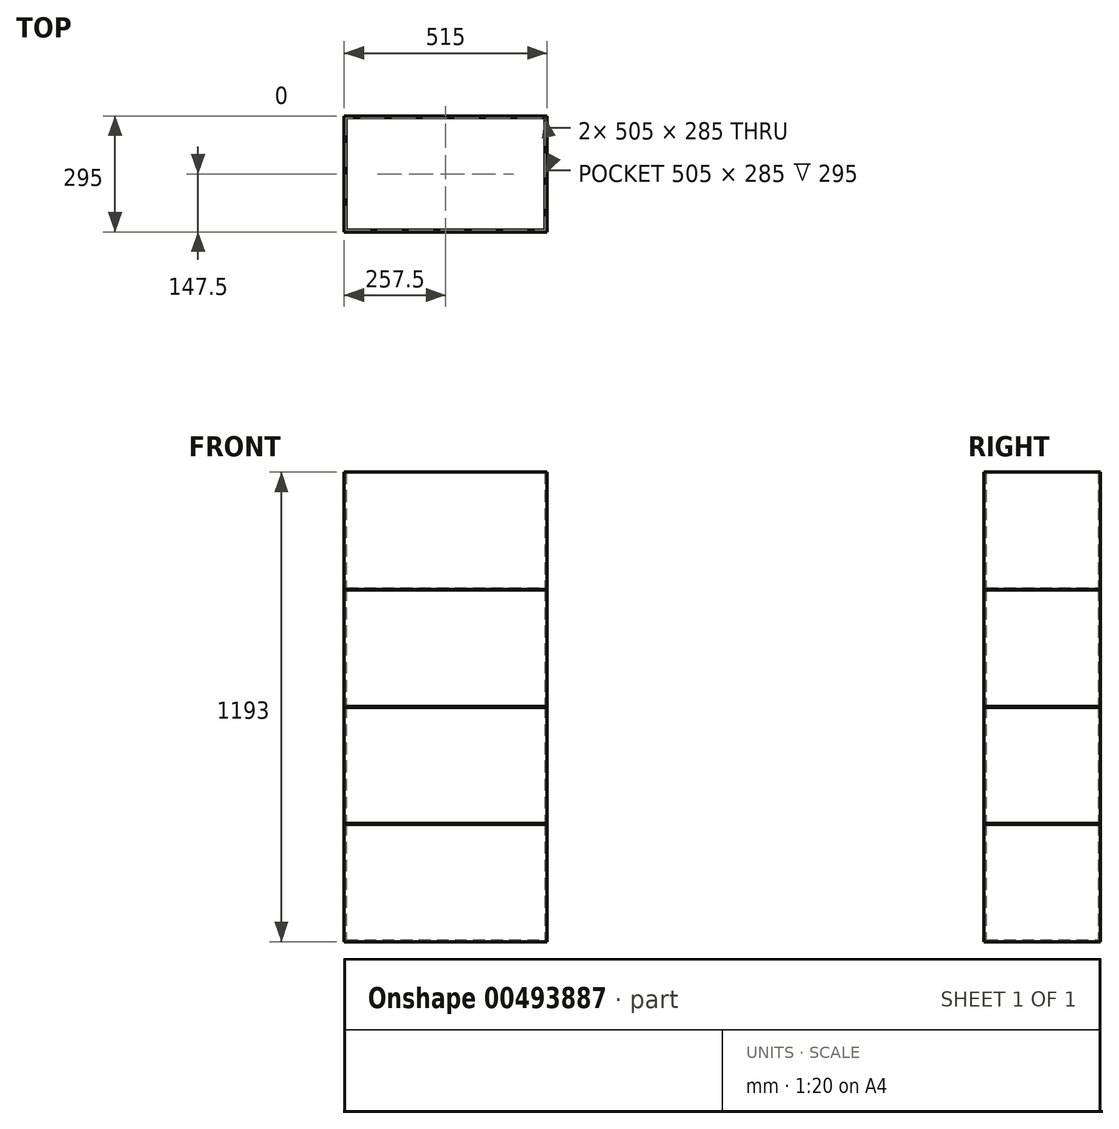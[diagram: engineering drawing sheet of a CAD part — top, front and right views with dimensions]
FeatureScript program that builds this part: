
annotation { "Feature Type Name" : "Feature", "Feature Type Description" : "" }
export const myFeature = defineFeature(function(context is Context, id is Id, definition is map)
    precondition{}
    {
        {
            var Q0;
            Q0=qCreatedBy(makeId("Top.planeOp"),FACE);
            var sketch = newSketch(context, id + "F0", { "sketchPlane" : qUnion([Q0])});
            skLineSegment(sketch, "E0.bottom", {"start": v(-257.5, -147.5) * mm, "end": v(257.5, -147.5) * mm});
            skLineSegment(sketch, "E0.top", {"start": v(-257.5, 147.5) * mm, "end": v(257.5, 147.5) * mm});
            skLineSegment(sketch, "E0.left", {"start": v(-257.5, -147.5) * mm, "end": v(-257.5, 147.5) * mm});
            skLineSegment(sketch, "E0.right", {"start": v(257.5, -147.5) * mm, "end": v(257.5, 147.5) * mm});
            skPoint(sketch, "E0.middle", {"position": v(0, 0) * mm});
            skSolve(sketch);
        }
        {
            var Q0;
            Q0=makeQuery(id+"F0.imprint","IMPRINT",FACE,{"disambiguationData":[TD([[makeQuery(id+"F0.imprint","IMPRINT",EDGE,{"derivedFrom":sQuery(id+"F0.wireOp",EDGE,"E0.bottom")}),1.0]])]});
            extrude(context, id + "F1", {"entities" : qUnion([Q0]), "depth" : 5 * mm});
        }
        {
            var Q0;
            Q0=makeQuery(id+"F1.opExtrude","CAP_FACE",FACE,{"disambiguationData":[OSD([sQuery(id+"F0.wireOp",EDGE,"E0.bottom"),sQuery(id+"F0.wireOp",EDGE,"E0.top"),sQuery(id+"F0.wireOp",EDGE,"E0.left"),sQuery(id+"F0.wireOp",EDGE,"E0.right")])],"isStart":false});
            var sketch = newSketch(context, id + "F2", { "sketchPlane" : qUnion([Q0])});
            skLineSegment(sketch, "E1.0", {"start": v(-257.5, 147.5) * mm, "end": v(257.5, 147.5) * mm});
            skLineSegment(sketch, "E2.0", {"start": v(-257.5, -147.5) * mm, "end": v(-257.5, 147.5) * mm});
            skLineSegment(sketch, "E3.0", {"start": v(257.5, -147.5) * mm, "end": v(257.5, 147.5) * mm});
            skLineSegment(sketch, "E4.0", {"start": v(-257.5, -147.5) * mm, "end": v(257.5, -147.5) * mm});
            skLineSegment(sketch, "E5.0", {"start": v(-252.5, 142.5) * mm, "end": v(252.5, 142.5) * mm});
            skLineSegment(sketch, "E5.1", {"start": v(-252.5, -142.5) * mm, "end": v(-252.5, 142.5) * mm});
            skLineSegment(sketch, "E5.2", {"start": v(-252.5, -142.5) * mm, "end": v(252.5, -142.5) * mm});
            skLineSegment(sketch, "E5.3", {"start": v(252.5, -142.5) * mm, "end": v(252.5, 142.5) * mm});
            skSolve(sketch);
        }
        {
            var Q0;
            Q0=makeQuery(id+"F2.imprint","IMPRINT",FACE,{"disambiguationData":[TD([[makeQuery(id+"F2.imprint","IMPRINT",EDGE,{"derivedFrom":sQuery(id+"F2.wireOp",EDGE,"E1.0")}),-1.0]])]});
            extrude(context, id + "F3", {"entities" : qUnion([Q0]), "operationType" : NewBodyOperationType.ADD, "depth" : 295 * mm});
        }
        {
            var Q0;
            Q0=makeQuery(id+"F1.opExtrude","SWEPT_BODY",BODY,{"disambiguationData":[OSD([sQuery(id+"F0.wireOp",EDGE,"E0.bottom"),sQuery(id+"F0.wireOp",EDGE,"E0.top"),sQuery(id+"F0.wireOp",EDGE,"E0.left"),sQuery(id+"F0.wireOp",EDGE,"E0.right")])]});
            transform(context, id + "F4", {"entities" : qUnion([Q0]), "transformType" : TransformType.TRANSLATION_3D, "dx" : 0 * mm, "dy" : 0 * mm, "dz" : 298 * mm, "makeCopy" : true});
        }
        {
            var Q0;
            Q0=makeQuery(id+"F1.opExtrude","SWEPT_BODY",BODY,{"disambiguationData":[OSD([sQuery(id+"F0.wireOp",EDGE,"E0.bottom"),sQuery(id+"F0.wireOp",EDGE,"E0.top"),sQuery(id+"F0.wireOp",EDGE,"E0.left"),sQuery(id+"F0.wireOp",EDGE,"E0.right")])]});
            transform(context, id + "F5", {"entities" : qUnion([Q0]), "transformType" : TransformType.TRANSLATION_3D, "dx" : 0 * mm, "dy" : 0 * mm, "dz" : 595 * mm, "makeCopy" : true});
        }
        {
            var Q0;
            Q0=makeQuery(id+"F1.opExtrude","SWEPT_BODY",BODY,{"disambiguationData":[OSD([sQuery(id+"F0.wireOp",EDGE,"E0.bottom"),sQuery(id+"F0.wireOp",EDGE,"E0.top"),sQuery(id+"F0.wireOp",EDGE,"E0.left"),sQuery(id+"F0.wireOp",EDGE,"E0.right")])]});
            transform(context, id + "F6", {"entities" : qUnion([Q0]), "transformType" : TransformType.TRANSLATION_3D, "dx" : 0 * mm, "dy" : 0 * mm, "dz" : 893 * mm, "makeCopy" : true});
        }
    });
